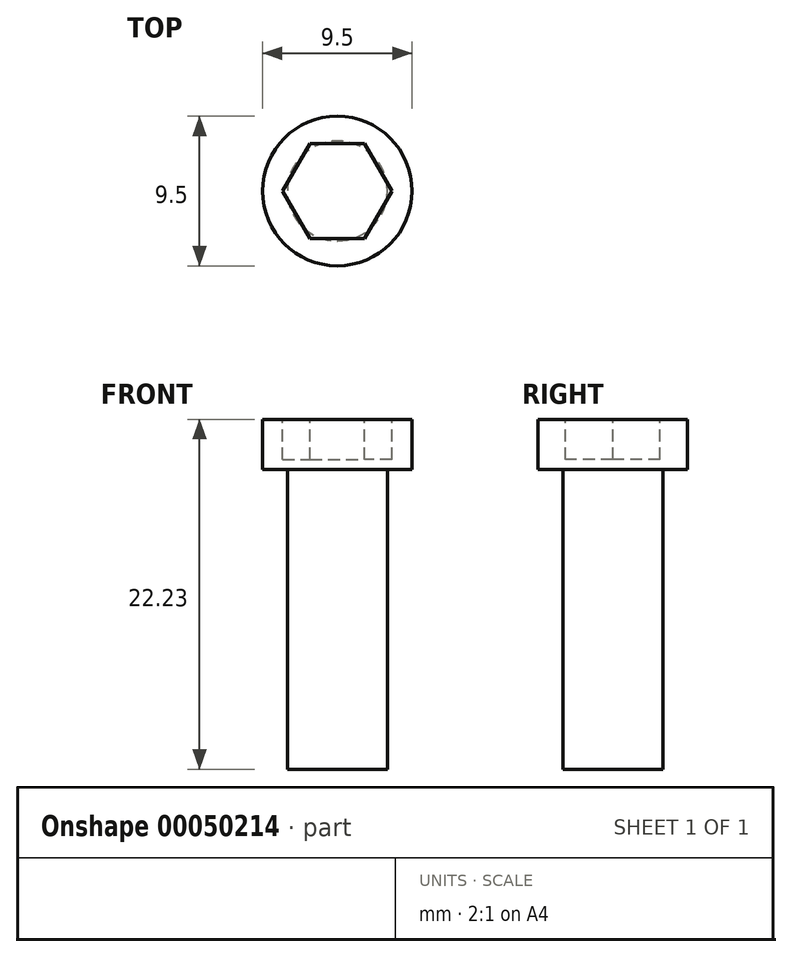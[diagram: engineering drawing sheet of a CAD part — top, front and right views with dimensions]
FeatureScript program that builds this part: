
annotation { "Feature Type Name" : "Feature", "Feature Type Description" : "" }
export const myFeature = defineFeature(function(context is Context, id is Id, definition is map)
    precondition{}
    {
        {
            var Q0;
            Q0=qCreatedBy(makeId("Front.planeOp"),FACE);
            var sketch = newSketch(context, id + "F0", { "sketchPlane" : qUnion([Q0])});
            skLineSegment(sketch, "E0", {"start": v(0, 0) * mm, "end": v(3.18, 0) * mm});
            skLineSegment(sketch, "E1", {"start": v(3.18, 0) * mm, "end": v(3.18, 19.05) * mm});
            skLineSegment(sketch, "E2", {"start": v(3.17, 19.05) * mm, "end": v(4.75, 19.05) * mm});
            skLineSegment(sketch, "E3", {"start": v(4.75, 19.05) * mm, "end": v(4.75, 22.23) * mm});
            skLineSegment(sketch, "E4", {"start": v(4.75, 22.23) * mm, "end": v(0, 22.23) * mm});
            skLineSegment(sketch, "E5", {"start": v(0, 22.23) * mm, "end": v(0, 0) * mm});
            skLineSegment(sketch, "E6", {"start": v(0, 32.16) * mm, "end": v(0, -8.29) * mm, "construction": true});
            skSolve(sketch);
        }
        {
            var Q0;
            Q0 = qSketchRegion(id + "F0", true);
            var Q1;
            Q1=sQuery(id+"F0.wireOp",EDGE,"E6");
            revolve(context, id + "F1", {"entities" : qUnion([Q0]), "axis" : qUnion([Q1]), "revolveType" : RevolveType.FULL});
        }
        {
            var Q0;
            Q0=makeQuery(id+"F1.opRevolve","SWEPT_FACE",FACE,{"disambiguationData":[OSD([sQuery(id+"F0.wireOp",EDGE,"E4")])]});
            var sketch = newSketch(context, id + "F2", { "sketchPlane" : qUnion([Q0])});
            skCircle(sketch, "E7.cCircle", {"center": v(0, 0) * mm, "radius": 3.47 * mm, "construction": true});
            skLineSegment(sketch, "E7.0", {"start": v(3.47, 0) * mm, "end": v(1.74, -3) * mm});
            skLineSegment(sketch, "E7.1", {"start": v(1.74, -3) * mm, "end": v(-1.74, -3) * mm});
            skLineSegment(sketch, "E7.2", {"start": v(-1.74, -3) * mm, "end": v(-3.47, 0) * mm});
            skLineSegment(sketch, "E7.3", {"start": v(-3.47, 0) * mm, "end": v(-1.74, 3) * mm});
            skLineSegment(sketch, "E7.4", {"start": v(-1.74, 3) * mm, "end": v(1.74, 3) * mm});
            skLineSegment(sketch, "E7.5", {"start": v(1.74, 3) * mm, "end": v(3.47, 0) * mm});
            skSolve(sketch);
        }
        {
            var Q0;
            Q0 = qSketchRegion(id + "F2", true);
            extrude(context, id + "F3", {"entities" : qUnion([Q0]), "operationType" : NewBodyOperationType.REMOVE, "oppositeDirection" : true, "depth" : 2.54 * mm});
        }
    });
